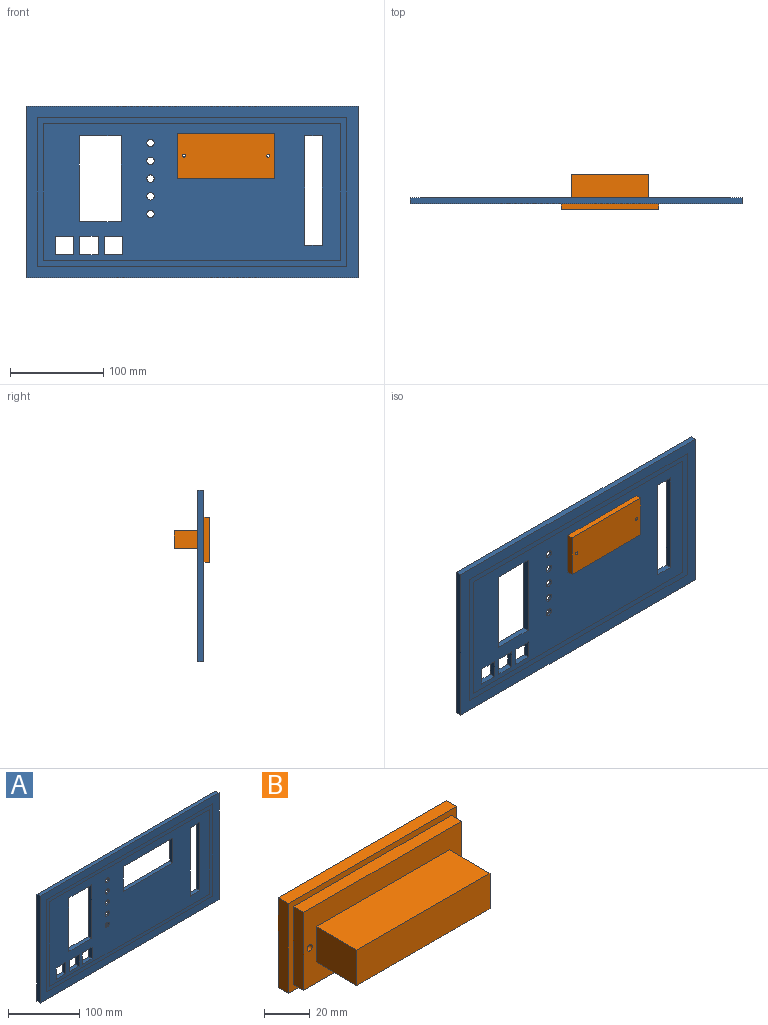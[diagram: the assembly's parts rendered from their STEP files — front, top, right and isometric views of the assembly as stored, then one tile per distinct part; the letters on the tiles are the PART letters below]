
ASSEMBLY  parts=2 mates=1
PART A: 52 faces, bbox 355.6x6.4x184.2 mm
  f0: plane 330.21x158.76mm, normal (0,-1,0), area 6048.4mm2, adj f11,f50
  f1: plane 330.2x158.75mm, normal (0,1,0), area 6048.4mm2, adj f2,f3,f4,f5,f45,f46,f47,f48
  f2: plane 146.05x3.96mm, normal (-1,0,0), area 578.7mm2, adj f1,f3,f5,f41
  f3: plane 317.5x3.96mm, normal (0,0,-1), area 1258.1mm2, adj f1,f2,f4,f41
  f4: plane 146.05x3.96mm, normal (1,0,0), area 578.7mm2, adj f1,f3,f5,f41
  f5: plane 317.5x3.96mm, normal (0,0,1), area 1258.1mm2, adj f1,f2,f4,f41
  f6: cylinder r=3.97mm len=7.94mm, axis (0,1,0), area 63.3mm2, adj f11,f12
  f7: cylinder r=3.97mm len=7.94mm, axis (0,1,0), area 63.3mm2, adj f11,f12
  f8: cylinder r=3.97mm len=7.94mm, axis (0,1,0), area 63.3mm2, adj f11,f12
  f9: cylinder r=3.97mm len=7.94mm, axis (0,1,0), area 63.3mm2, adj f11,f12
  f10: cylinder r=3.97mm len=7.94mm, axis (0,1,0), area 63.3mm2, adj f11,f12
  f11: plane 317.51x146.06mm, normal (0,-1,0), area 34378.5mm2, adj f0,f6,f7,f8,f9,f10,f16,f17
  f12: plane 90.71x14.29mm, normal (0,1,0), area 1004.2mm2, adj f6,f7,f8,f9,f10,f13,f14,f15
  f13: cylinder r=7.14mm len=14.29mm, axis (0,1,0), area 86.3mm2, adj f12,f14,f40,f41
  f14: plane 76.2x3.81mm, normal (-1,0,0), area 290.3mm2, adj f12,f13,f15,f41
  f15: cylinder r=7.14mm len=14.28mm, axis (0,1,0), area 84.1mm2, adj f12,f14,f40,f41
  f16: plane 117.48x6.35mm, normal (1,0,0), area 746mm2, adj f11,f17,f34,f41
  f17: plane 19.05x6.35mm, normal (0,0,-1), area 121mm2, adj f11,f16,f18,f41
  f18: plane 117.48x6.35mm, normal (-1,0,0), area 746mm2, adj f11,f17,f34,f41
  f19: plane 42.88x6.35mm, normal (1,0,0), area 272.3mm2, adj f11,f20,f35,f41
  f20: plane 98.43x6.35mm, normal (0,0,-1), area 625mm2, adj f11,f19,f21,f41
  f21: plane 42.88x6.35mm, normal (-1,0,0), area 272.3mm2, adj f11,f20,f35,f41
  f22: plane 92.08x6.35mm, normal (1,0,0), area 584.7mm2, adj f11,f23,f36,f41
  f23: plane 44.96x6.35mm, normal (0,0,-1), area 285.5mm2, adj f11,f22,f24,f41
  f24: plane 92.08x6.35mm, normal (-1,0,0), area 584.7mm2, adj f11,f23,f36,f41
  f25: plane 19.56x6.35mm, normal (1,0,0), area 124.2mm2, adj f11,f26,f37,f41
  f26: plane 19.56x6.35mm, normal (0,0,-1), area 124.2mm2, adj f11,f25,f27,f41
  f27: plane 19.56x6.35mm, normal (-1,0,0), area 124.2mm2, adj f11,f26,f37,f41
  f28: plane 19.56x6.35mm, normal (1,0,0), area 124.2mm2, adj f11,f29,f38,f41
  f29: plane 19.56x6.35mm, normal (0,0,-1), area 124.2mm2, adj f11,f28,f30,f41
  f30: plane 19.56x6.35mm, normal (-1,0,0), area 124.2mm2, adj f11,f29,f38,f41
  f31: plane 19.56x6.35mm, normal (1,0,0), area 124.2mm2, adj f11,f32,f39,f41
  f32: plane 19.56x6.35mm, normal (0,0,-1), area 124.2mm2, adj f11,f31,f33,f41
  f33: plane 19.56x6.35mm, normal (-1,0,0), area 124.2mm2, adj f11,f32,f39,f41
  f34: plane 19.05x6.35mm, normal (0,0,1), area 121mm2, adj f11,f16,f18,f41
  f35: plane 98.43x6.35mm, normal (0,0,1), area 625mm2, adj f11,f19,f21,f41
  f36: plane 44.96x6.35mm, normal (0,0,1), area 285.5mm2, adj f11,f22,f24,f41
  f37: plane 19.56x6.35mm, normal (0,0,1), area 124.2mm2, adj f11,f25,f27,f41
  f38: plane 19.56x6.35mm, normal (0,0,1), area 124.2mm2, adj f11,f28,f30,f41
  f39: plane 19.56x6.35mm, normal (0,0,1), area 124.2mm2, adj f11,f31,f33,f41
  f40: plane 76.79x3.81mm, normal (1,0,0), area 292.6mm2, adj f12,f13,f15,f41
  f41: plane 317.5x146.05mm, normal (0,1,0), area 33374.3mm2, adj f2,f3,f4,f5,f13,f14,f15,f16
  f42: plane 355.6x6.35mm, normal (0,0,1), area 2258.1mm2, adj f43,f49,f50,f51
  f43: plane 184.15x6.35mm, normal (-1,0,0), area 1169.4mm2, adj f42,f44,f50,f51
  f44: plane 355.6x6.35mm, normal (0,0,-1), area 2258.1mm2, adj f43,f49,f50,f51
  f45: plane 330.2x3.96mm, normal (0,0,1), area 1308.4mm2, adj f1,f46,f48,f51
  f46: plane 158.75x3.96mm, normal (1,0,0), area 629mm2, adj f1,f45,f47,f51
  f47: plane 330.2x3.96mm, normal (0,0,-1), area 1308.4mm2, adj f1,f46,f48,f51
  f48: plane 158.75x3.96mm, normal (-1,0,0), area 629mm2, adj f1,f45,f47,f51
  f49: plane 184.15x6.35mm, normal (1,0,0), area 1169.4mm2, adj f42,f44,f50,f51
  f50: plane 355.61x184.16mm, normal (0,-1,0), area 13064.5mm2, adj f0,f42,f43,f44,f49
  f51: plane 355.6x184.15mm, normal (0,1,0), area 13064.5mm2, adj f42,f43,f44,f45,f46,f47,f48,f49
PART B: 18 faces, bbox 104.4x38.1x48.3 mm
  f0: plane 48.26x6.35mm, normal (1,0,0), area 306.5mm2, adj f1,f3,f4,f5
  f1: plane 104.39x6.35mm, normal (0,0,1), area 662.9mm2, adj f0,f2,f4,f5
  f2: plane 48.26x6.35mm, normal (-1,0,0), area 306.5mm2, adj f1,f3,f4,f5
  f3: plane 104.39x6.35mm, normal (0,0,-1), area 662.9mm2, adj f0,f2,f4,f5
  f4: plane 104.39x48.26mm, normal (0,-1,0), area 929mm2, adj f0,f1,f2,f3,f6,f7,f8,f11
  f5: plane 104.39x48.26mm, normal (0,1,0), area 5022.2mm2, adj f0,f1,f2,f3,f9,f10
  f6: plane 98.04x6.35mm, normal (0,0,1), area 622.6mm2, adj f4,f7,f11,f12
  f7: plane 41.91x6.35mm, normal (-1,0,0), area 266.1mm2, adj f4,f6,f8,f12
  f8: plane 98.04x6.35mm, normal (0,0,-1), area 622.6mm2, adj f4,f7,f11,f12
  f9: cylinder r=1.59mm len=12.7mm, axis (0,1,0), area 126.7mm2, adj f5,f12
  f10: cylinder r=1.59mm len=12.7mm, axis (0,1,0), area 126.7mm2, adj f5,f12
  f11: plane 41.91x6.35mm, normal (1,0,0), area 266.1mm2, adj f4,f6,f8,f12
  f12: plane 98.04x41.91mm, normal (0,-1,0), area 2520.6mm2, adj f6,f7,f8,f9,f10,f11,f14,f15
  f13: plane 82.55x19.05mm, normal (0,-1,0), area 1572.6mm2, adj f14,f15,f16,f17
  f14: plane 25.4x19.05mm, normal (1,0,0), area 483.9mm2, adj f12,f13,f15,f17
  f15: plane 82.55x25.4mm, normal (0,0,-1), area 2096.8mm2, adj f12,f13,f14,f16
  f16: plane 25.4x19.05mm, normal (-1,0,0), area 483.9mm2, adj f12,f13,f15,f17
  f17: plane 82.55x25.4mm, normal (0,0,1), area 2096.8mm2, adj f12,f13,f14,f16
PLACE A t=(-35.2,217.95,-9.32)mm
PLACE B rot(axis=(-1,0,0),180deg) t=(2.24,205.07,23.01)mm
MATE slider A.f11 <-> B.f5  axis (0,-1,0) through (1.31,211.6,29.56)mm
